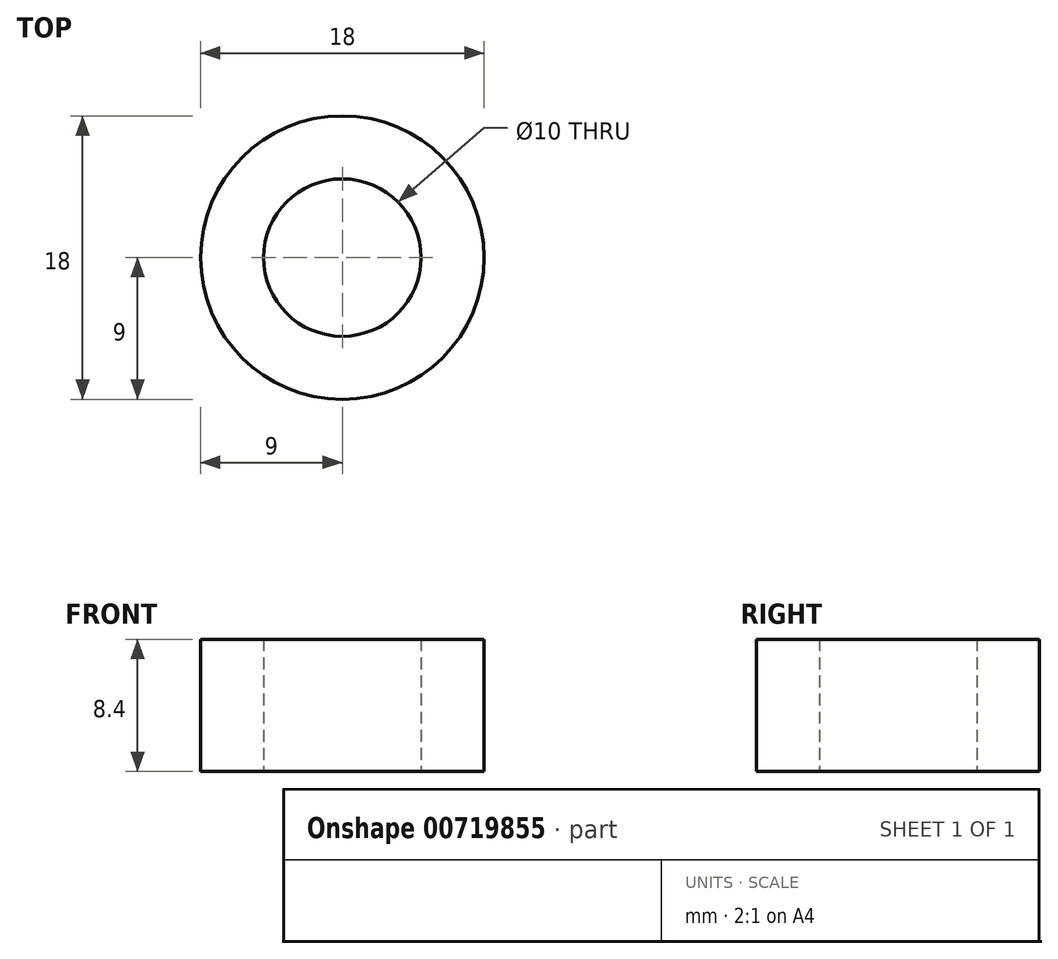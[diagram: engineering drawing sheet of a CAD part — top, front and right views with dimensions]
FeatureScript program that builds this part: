
annotation { "Feature Type Name" : "Feature", "Feature Type Description" : "" }
export const myFeature = defineFeature(function(context is Context, id is Id, definition is map)
    precondition{}
    {
        {
            var Q0;
            Q0=qCreatedBy(makeId("Top.planeOp"),FACE);
            var sketch = newSketch(context, id + "F0", { "sketchPlane" : qUnion([Q0])});
            skCircle(sketch, "E0", {"center": v(0, 0) * mm, "radius": 9 * mm});
            skCircle(sketch, "E1", {"center": v(0, 0) * mm, "radius": 5 * mm});
            skSolve(sketch);
        }
        {
            var Q0;
            Q0=makeQuery(id+"F0.imprint","IMPRINT",FACE,{"disambiguationData":[TD([[makeQuery(id+"F0.imprint","IMPRINT",EDGE,{"derivedFrom":sQuery(id+"F0.wireOp",EDGE,"E0")}),1.0]])]});
            extrude(context, id + "F1", {"entities" : qUnion([Q0]), "depth" : 8.4 * mm, "offsetDistance" : 25 * mm});
        }
    });
